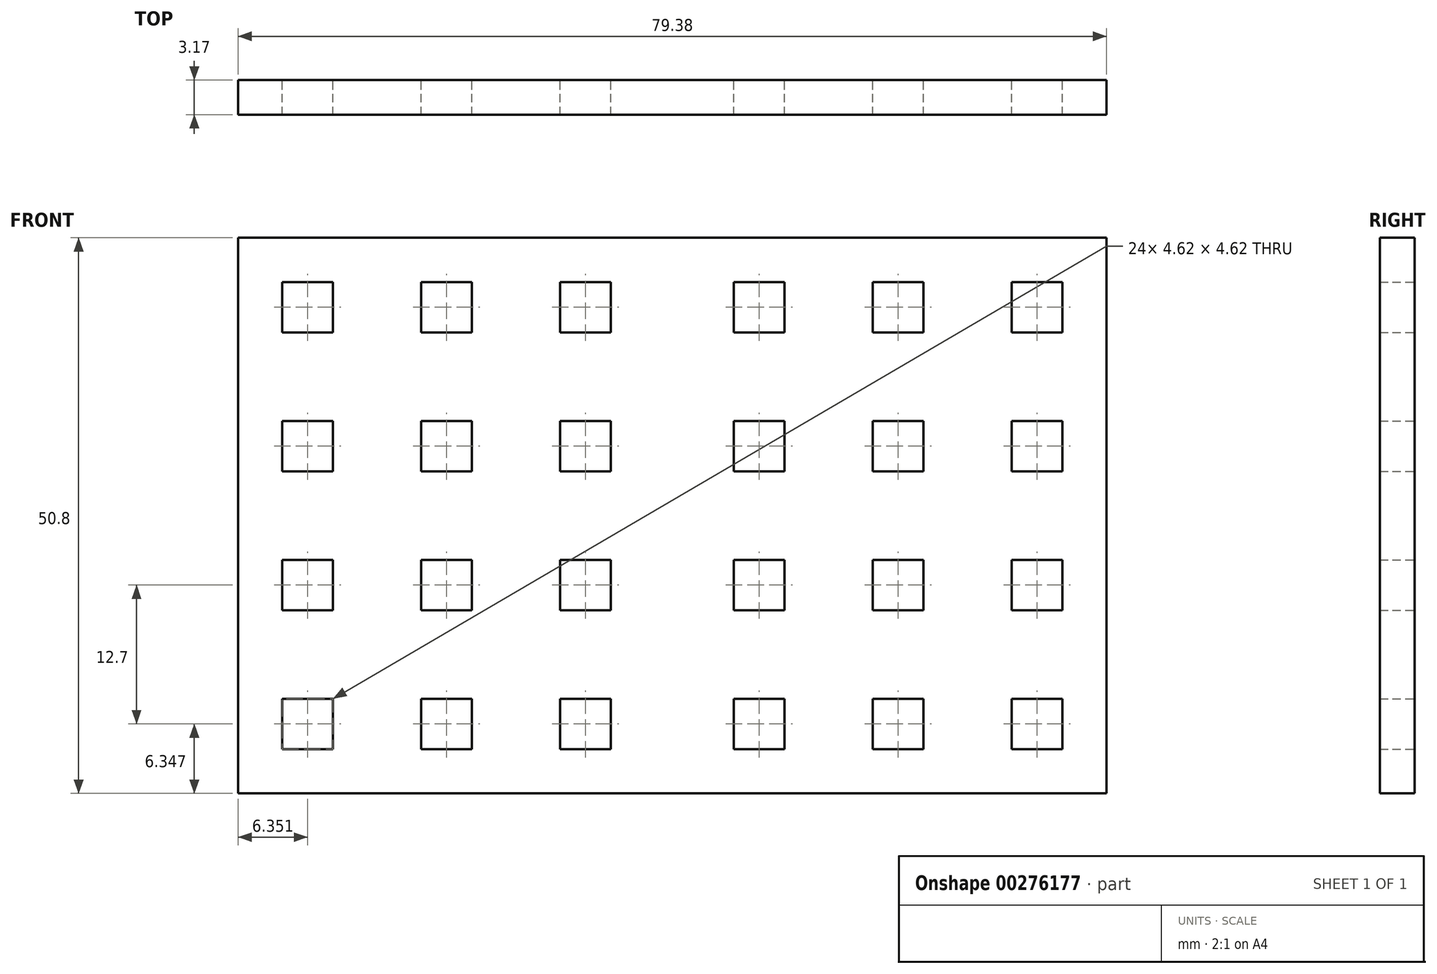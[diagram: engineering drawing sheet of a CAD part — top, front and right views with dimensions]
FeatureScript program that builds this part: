
annotation { "Feature Type Name" : "Feature", "Feature Type Description" : "" }
export const myFeature = defineFeature(function(context is Context, id is Id, definition is map)
    precondition{}
    {
        {
            var Q0;
            Q0=qCreatedBy(makeId("Front.planeOp"),FACE);
            var sketch = newSketch(context, id + "F0", { "sketchPlane" : qUnion([Q0])});
            skLineSegment(sketch, "E0.bottom", {"start": v(-41.7, 18.96) * mm, "end": v(37.68, 18.96) * mm});
            skLineSegment(sketch, "E0.top", {"start": v(-41.7, -31.84) * mm, "end": v(37.68, -31.84) * mm});
            skLineSegment(sketch, "E0.left", {"start": v(-41.7, 18.96) * mm, "end": v(-41.7, -31.84) * mm});
            skLineSegment(sketch, "E0.right", {"start": v(37.68, 18.96) * mm, "end": v(37.68, -31.84) * mm});
            skLineSegment(sketch, "E1.bottom", {"start": v(-37.66, 14.92) * mm, "end": v(-33.04, 14.92) * mm});
            skLineSegment(sketch, "E1.top", {"start": v(-37.66, 10.3) * mm, "end": v(-33.04, 10.3) * mm});
            skLineSegment(sketch, "E1.left", {"start": v(-37.66, 14.92) * mm, "end": v(-37.66, 10.3) * mm});
            skLineSegment(sketch, "E1.right", {"start": v(-33.04, 14.92) * mm, "end": v(-33.04, 10.3) * mm});
            skLineSegment(sketch, "E2.0.1.0", {"start": v(-37.66, 2.22) * mm, "end": v(-33.04, 2.22) * mm});
            skLineSegment(sketch, "E2.0.1.1", {"start": v(-37.66, 2.22) * mm, "end": v(-37.66, -2.4) * mm});
            skLineSegment(sketch, "E2.0.1.2", {"start": v(-37.66, -2.4) * mm, "end": v(-33.04, -2.4) * mm});
            skLineSegment(sketch, "E2.0.1.3", {"start": v(-33.04, 2.22) * mm, "end": v(-33.04, -2.4) * mm});
            skLineSegment(sketch, "E2.0.2.0", {"start": v(-37.66, -10.48) * mm, "end": v(-33.04, -10.48) * mm});
            skLineSegment(sketch, "E2.0.2.1", {"start": v(-37.66, -10.48) * mm, "end": v(-37.66, -15.1) * mm});
            skLineSegment(sketch, "E2.0.2.2", {"start": v(-37.66, -15.1) * mm, "end": v(-33.04, -15.1) * mm});
            skLineSegment(sketch, "E2.0.2.3", {"start": v(-33.04, -10.48) * mm, "end": v(-33.04, -15.1) * mm});
            skLineSegment(sketch, "E2.0.3.0", {"start": v(-37.66, -23.18) * mm, "end": v(-33.04, -23.18) * mm});
            skLineSegment(sketch, "E2.0.3.1", {"start": v(-37.66, -23.18) * mm, "end": v(-37.66, -27.8) * mm});
            skLineSegment(sketch, "E2.0.3.2", {"start": v(-37.66, -27.8) * mm, "end": v(-33.04, -27.8) * mm});
            skLineSegment(sketch, "E2.0.3.3", {"start": v(-33.04, -23.18) * mm, "end": v(-33.04, -27.8) * mm});
            skLineSegment(sketch, "E2.1.0.0", {"start": v(-24.96, 14.92) * mm, "end": v(-20.34, 14.92) * mm});
            skLineSegment(sketch, "E2.1.0.1", {"start": v(-24.96, 14.92) * mm, "end": v(-24.96, 10.3) * mm});
            skLineSegment(sketch, "E2.1.0.2", {"start": v(-24.96, 10.3) * mm, "end": v(-20.34, 10.3) * mm});
            skLineSegment(sketch, "E2.1.0.3", {"start": v(-20.34, 14.92) * mm, "end": v(-20.34, 10.3) * mm});
            skLineSegment(sketch, "E2.1.1.0", {"start": v(-24.96, 2.22) * mm, "end": v(-20.34, 2.22) * mm});
            skLineSegment(sketch, "E2.1.1.1", {"start": v(-24.96, 2.22) * mm, "end": v(-24.96, -2.4) * mm});
            skLineSegment(sketch, "E2.1.1.2", {"start": v(-24.96, -2.4) * mm, "end": v(-20.34, -2.4) * mm});
            skLineSegment(sketch, "E2.1.1.3", {"start": v(-20.34, 2.22) * mm, "end": v(-20.34, -2.4) * mm});
            skLineSegment(sketch, "E2.1.2.0", {"start": v(-24.96, -10.48) * mm, "end": v(-20.34, -10.48) * mm});
            skLineSegment(sketch, "E2.1.2.1", {"start": v(-24.96, -10.48) * mm, "end": v(-24.96, -15.1) * mm});
            skLineSegment(sketch, "E2.1.2.2", {"start": v(-24.96, -15.1) * mm, "end": v(-20.34, -15.1) * mm});
            skLineSegment(sketch, "E2.1.2.3", {"start": v(-20.34, -10.48) * mm, "end": v(-20.34, -15.1) * mm});
            skLineSegment(sketch, "E2.1.3.0", {"start": v(-24.96, -23.18) * mm, "end": v(-20.34, -23.18) * mm});
            skLineSegment(sketch, "E2.1.3.1", {"start": v(-24.96, -23.18) * mm, "end": v(-24.96, -27.8) * mm});
            skLineSegment(sketch, "E2.1.3.2", {"start": v(-24.96, -27.8) * mm, "end": v(-20.34, -27.8) * mm});
            skLineSegment(sketch, "E2.1.3.3", {"start": v(-20.34, -23.18) * mm, "end": v(-20.34, -27.8) * mm});
            skLineSegment(sketch, "E2.2.0.0", {"start": v(-12.26, 14.92) * mm, "end": v(-7.64, 14.92) * mm});
            skLineSegment(sketch, "E2.2.0.1", {"start": v(-12.26, 14.92) * mm, "end": v(-12.26, 10.3) * mm});
            skLineSegment(sketch, "E2.2.0.2", {"start": v(-12.26, 10.3) * mm, "end": v(-7.64, 10.3) * mm});
            skLineSegment(sketch, "E2.2.0.3", {"start": v(-7.64, 14.92) * mm, "end": v(-7.64, 10.3) * mm});
            skLineSegment(sketch, "E2.2.1.0", {"start": v(-12.26, 2.22) * mm, "end": v(-7.64, 2.22) * mm});
            skLineSegment(sketch, "E2.2.1.1", {"start": v(-12.26, 2.22) * mm, "end": v(-12.26, -2.4) * mm});
            skLineSegment(sketch, "E2.2.1.2", {"start": v(-12.26, -2.4) * mm, "end": v(-7.64, -2.4) * mm});
            skLineSegment(sketch, "E2.2.1.3", {"start": v(-7.64, 2.22) * mm, "end": v(-7.64, -2.4) * mm});
            skLineSegment(sketch, "E2.2.2.0", {"start": v(-12.26, -10.48) * mm, "end": v(-7.64, -10.48) * mm});
            skLineSegment(sketch, "E2.2.2.1", {"start": v(-12.26, -10.48) * mm, "end": v(-12.26, -15.1) * mm});
            skLineSegment(sketch, "E2.2.2.2", {"start": v(-12.26, -15.1) * mm, "end": v(-7.64, -15.1) * mm});
            skLineSegment(sketch, "E2.2.2.3", {"start": v(-7.64, -10.48) * mm, "end": v(-7.64, -15.1) * mm});
            skLineSegment(sketch, "E2.2.3.0", {"start": v(-12.26, -23.18) * mm, "end": v(-7.64, -23.18) * mm});
            skLineSegment(sketch, "E2.2.3.1", {"start": v(-12.26, -23.18) * mm, "end": v(-12.26, -27.8) * mm});
            skLineSegment(sketch, "E2.2.3.2", {"start": v(-12.26, -27.8) * mm, "end": v(-7.64, -27.8) * mm});
            skLineSegment(sketch, "E2.2.3.3", {"start": v(-7.64, -23.18) * mm, "end": v(-7.64, -27.8) * mm});
            skLineSegment(sketch, "E2.direction1", {"start": v(-37.66, 14.92) * mm, "end": v(-24.96, 14.92) * mm, "construction": true});
            skLineSegment(sketch, "E2.direction2", {"start": v(-37.66, 14.92) * mm, "end": v(-37.66, 2.22) * mm, "construction": true});
            skLineSegment(sketch, "E3", {"start": v(-41.7, 18.96) * mm, "end": v(-2.01, 18.96) * mm});
            skLineSegment(sketch, "E4.MirrorCS", {"start": v(20.94, -10.48) * mm, "end": v(20.94, -15.1) * mm});
            skLineSegment(sketch, "E5.MirrorCS", {"start": v(33.64, -10.48) * mm, "end": v(33.64, -15.1) * mm});
            skLineSegment(sketch, "E6.MirrorCS", {"start": v(29.01, -10.48) * mm, "end": v(29.01, -15.1) * mm});
            skLineSegment(sketch, "E7.MirrorCS", {"start": v(3.61, -10.48) * mm, "end": v(3.61, -15.1) * mm});
            skLineSegment(sketch, "E8.MirrorCS", {"start": v(16.31, -10.48) * mm, "end": v(16.31, -15.1) * mm});
            skLineSegment(sketch, "E9.MirrorCS", {"start": v(8.24, -10.48) * mm, "end": v(8.24, -15.1) * mm});
            skLineSegment(sketch, "E10.MirrorCS", {"start": v(33.64, 14.92) * mm, "end": v(33.64, 10.3) * mm});
            skLineSegment(sketch, "E11.MirrorCS", {"start": v(33.64, 14.92) * mm, "end": v(29.01, 14.92) * mm});
            skLineSegment(sketch, "E12.MirrorCS", {"start": v(33.64, 14.92) * mm, "end": v(20.94, 14.92) * mm, "construction": true});
            skLineSegment(sketch, "E13.MirrorCS", {"start": v(33.64, 10.3) * mm, "end": v(29.01, 10.3) * mm});
            skLineSegment(sketch, "E14.MirrorCS", {"start": v(8.24, -2.4) * mm, "end": v(3.61, -2.4) * mm});
            skLineSegment(sketch, "E15.MirrorCS", {"start": v(20.94, -2.4) * mm, "end": v(16.31, -2.4) * mm});
            skLineSegment(sketch, "E16.MirrorCS", {"start": v(16.31, -23.18) * mm, "end": v(16.31, -27.8) * mm});
            skLineSegment(sketch, "E17.MirrorCS", {"start": v(20.94, -23.18) * mm, "end": v(16.31, -23.18) * mm});
            skLineSegment(sketch, "E18.MirrorCS", {"start": v(33.64, -15.1) * mm, "end": v(29.01, -15.1) * mm});
            skLineSegment(sketch, "E19.MirrorCS", {"start": v(8.24, 14.92) * mm, "end": v(8.24, 10.3) * mm});
            skLineSegment(sketch, "E20.MirrorCS", {"start": v(20.94, -15.1) * mm, "end": v(16.31, -15.1) * mm});
            skLineSegment(sketch, "E21.MirrorCS", {"start": v(33.64, -23.18) * mm, "end": v(33.64, -27.8) * mm});
            skLineSegment(sketch, "E22.MirrorCS", {"start": v(33.64, 2.22) * mm, "end": v(29.01, 2.22) * mm});
            skLineSegment(sketch, "E23.MirrorCS", {"start": v(33.64, 2.22) * mm, "end": v(33.64, -2.4) * mm});
            skLineSegment(sketch, "E24.MirrorCS", {"start": v(3.61, 14.92) * mm, "end": v(3.61, 10.3) * mm});
            skLineSegment(sketch, "E25.MirrorCS", {"start": v(16.31, 14.92) * mm, "end": v(16.31, 10.3) * mm});
            skLineSegment(sketch, "E26.MirrorCS", {"start": v(8.24, 14.92) * mm, "end": v(3.61, 14.92) * mm});
            skLineSegment(sketch, "E27.MirrorCS", {"start": v(33.64, -23.18) * mm, "end": v(29.01, -23.18) * mm});
            skLineSegment(sketch, "E28.MirrorCS", {"start": v(8.24, -23.18) * mm, "end": v(3.61, -23.18) * mm});
            skLineSegment(sketch, "E29.MirrorCS", {"start": v(29.01, 14.92) * mm, "end": v(29.01, 10.3) * mm});
            skLineSegment(sketch, "E30.MirrorCS", {"start": v(8.24, -23.18) * mm, "end": v(8.24, -27.8) * mm});
            skLineSegment(sketch, "E31.MirrorCS", {"start": v(8.24, -10.48) * mm, "end": v(3.61, -10.48) * mm});
            skLineSegment(sketch, "E32.MirrorCS", {"start": v(20.94, -23.18) * mm, "end": v(20.94, -27.8) * mm});
            skLineSegment(sketch, "E33.MirrorCS", {"start": v(20.94, -10.48) * mm, "end": v(16.31, -10.48) * mm});
            skLineSegment(sketch, "E34.MirrorCS", {"start": v(8.24, 2.22) * mm, "end": v(3.61, 2.22) * mm});
            skLineSegment(sketch, "E35.MirrorCS", {"start": v(20.94, 2.22) * mm, "end": v(16.31, 2.22) * mm});
            skLineSegment(sketch, "E36.MirrorCS", {"start": v(20.94, 14.92) * mm, "end": v(20.94, 10.3) * mm});
            skLineSegment(sketch, "E37.MirrorCS", {"start": v(8.24, -15.1) * mm, "end": v(3.61, -15.1) * mm});
            skLineSegment(sketch, "E38.MirrorCS", {"start": v(33.64, 14.92) * mm, "end": v(33.64, 2.22) * mm, "construction": true});
            skLineSegment(sketch, "E39.MirrorCS", {"start": v(8.24, 2.22) * mm, "end": v(8.24, -2.4) * mm});
            skLineSegment(sketch, "E40.MirrorCS", {"start": v(33.64, -2.4) * mm, "end": v(29.01, -2.4) * mm});
            skLineSegment(sketch, "E41.MirrorCS", {"start": v(20.94, 2.22) * mm, "end": v(20.94, -2.4) * mm});
            skLineSegment(sketch, "E42.MirrorCS", {"start": v(29.01, -23.18) * mm, "end": v(29.01, -27.8) * mm});
            skLineSegment(sketch, "E43.MirrorCS", {"start": v(20.94, 10.3) * mm, "end": v(16.31, 10.3) * mm});
            skLineSegment(sketch, "E44.MirrorCS", {"start": v(3.61, -23.18) * mm, "end": v(3.61, -27.8) * mm});
            skLineSegment(sketch, "E45.MirrorCS", {"start": v(29.01, 2.22) * mm, "end": v(29.01, -2.4) * mm});
            skLineSegment(sketch, "E46.MirrorCS", {"start": v(8.24, 10.3) * mm, "end": v(3.61, 10.3) * mm});
            skLineSegment(sketch, "E47.MirrorCS", {"start": v(33.64, -27.8) * mm, "end": v(29.01, -27.8) * mm});
            skLineSegment(sketch, "E48.MirrorCS", {"start": v(33.64, -10.48) * mm, "end": v(29.01, -10.48) * mm});
            skLineSegment(sketch, "E49.MirrorCS", {"start": v(3.61, 2.22) * mm, "end": v(3.61, -2.4) * mm});
            skLineSegment(sketch, "E50.MirrorCS", {"start": v(16.31, 2.22) * mm, "end": v(16.31, -2.4) * mm});
            skLineSegment(sketch, "E51.MirrorCS", {"start": v(20.94, 14.92) * mm, "end": v(16.31, 14.92) * mm});
            skLineSegment(sketch, "E52.MirrorCS", {"start": v(20.94, -27.8) * mm, "end": v(16.31, -27.8) * mm});
            skLineSegment(sketch, "E53.MirrorCS", {"start": v(8.24, -27.8) * mm, "end": v(3.61, -27.8) * mm});
            skLineSegment(sketch, "E54", {"start": v(-2.01, 18.96) * mm, "end": v(-2.01, 8.45) * mm});
            skSolve(sketch);
        }
        {
            var Q0;
            Q0=makeQuery(id+"F0.imprint","IMPRINT",FACE,{"disambiguationData":[TD([[makeQuery(id+"F0.imprint","IMPRINT",EDGE,{"derivedFrom":sQuery(id+"F0.wireOp",EDGE,"E0.bottom")}),-1.0]])]});
            extrude(context, id + "F1", {"entities" : qUnion([Q0]), "depth" : 3.17 * mm});
        }
    });
